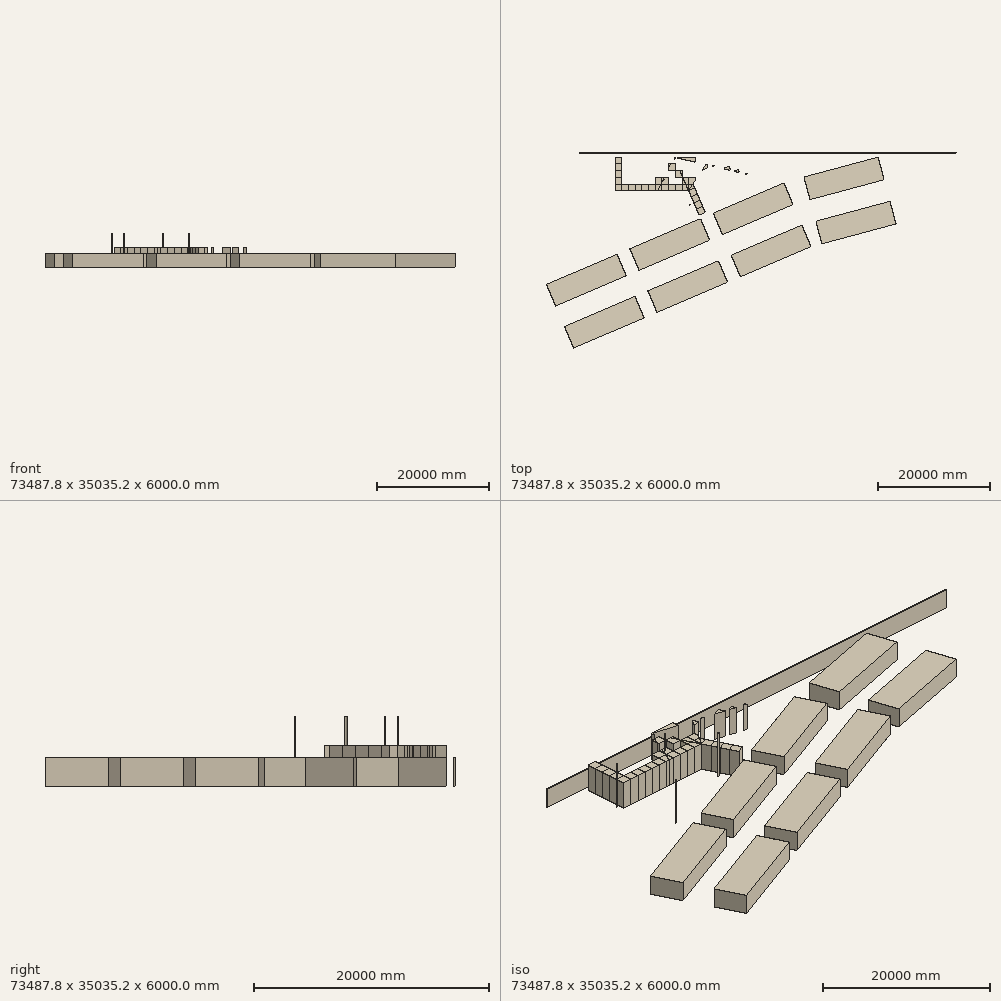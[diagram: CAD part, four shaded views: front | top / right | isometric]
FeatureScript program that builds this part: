
annotation { "Feature Type Name" : "Feature", "Feature Type Description" : "" }
export const myFeature = defineFeature(function(context is Context, id is Id, definition is map)
    precondition{}
    {
        {
            var Q0;
            Q0=qCreatedBy(makeId("Top.planeOp"),FACE);
            var sketch = newSketch(context, id + "F0", { "sketchPlane" : qUnion([Q0])});
            skLineSegment(sketch, "E0", {"start": v(21997.79, -272.27) * mm, "end": v(9345.13, -5680.4) * mm});
            skLineSegment(sketch, "E1", {"start": v(21997.79, -272.27) * mm, "end": v(20347.05, 3589.73) * mm});
            skLineSegment(sketch, "E2", {"start": v(20347.05, 3589.73) * mm, "end": v(7694.4, -1818.39) * mm});
            skLineSegment(sketch, "E3", {"start": v(7694.4, -1818.39) * mm, "end": v(9345.13, -5680.4) * mm});
            skLineSegment(sketch, "E4", {"start": v(7046.31, -6662.97) * mm, "end": v(5395.58, -2800.97) * mm});
            skLineSegment(sketch, "E5", {"start": v(5395.58, -2800.97) * mm, "end": v(-7257.08, -8209.09) * mm});
            skLineSegment(sketch, "E6", {"start": v(-7257.08, -8209.09) * mm, "end": v(-5606.35, -12071.09) * mm});
            skLineSegment(sketch, "E7", {"start": v(-7905.16, -13053.67) * mm, "end": v(-9555.9, -9191.67) * mm});
            skLineSegment(sketch, "E8", {"start": v(-9555.9, -9191.67) * mm, "end": v(-22208.56, -14599.78) * mm});
            skLineSegment(sketch, "E9", {"start": v(-22208.56, -14599.78) * mm, "end": v(-20557.82, -18461.79) * mm});
            skLineSegment(sketch, "E10.bottom", {"start": v(-9920.8, 8833.33) * mm, "end": v(51279.2, 8833.33) * mm});
            skLineSegment(sketch, "E10.top", {"start": v(-9920.8, 8233.33) * mm, "end": v(51279.2, 8233.33) * mm});
            skLineSegment(sketch, "E10.left", {"start": v(-9920.8, 8833.33) * mm, "end": v(-9920.8, 8233.33) * mm});
            skLineSegment(sketch, "E10.right", {"start": v(51279.2, 8833.33) * mm, "end": v(51279.2, 8233.33) * mm});
            skLineSegment(sketch, "E11", {"start": v(20347.05, 3589.73) * mm, "end": v(18362.24, 8233.33) * mm});
            skLineSegment(sketch, "E12", {"start": v(5395.58, -2800.97) * mm, "end": v(679.2, 8233.33) * mm});
            skLineSegment(sketch, "E13", {"start": v(-7257.08, -8209.09) * mm, "end": v(679.2, 8233.33) * mm});
            skLineSegment(sketch, "E14", {"start": v(679.2, 8233.33) * mm, "end": v(20347.05, 3589.73) * mm});
            skLineSegment(sketch, "E15", {"start": v(-9920.8, 8233.33) * mm, "end": v(13764.84, 8233.33) * mm});
            skLineSegment(sketch, "E16", {"start": v(13764.84, 8233.33) * mm, "end": v(16200.05, 2536) * mm});
            skLineSegment(sketch, "E17", {"start": v(5165.75, -2180.39) * mm, "end": v(3279.2, 2233.33) * mm});
            skLineSegment(sketch, "E18", {"start": v(3279.2, 2233.33) * mm, "end": v(-9920.8, 2233.33) * mm});
            skLineSegment(sketch, "E19", {"start": v(-9920.8, 2233.33) * mm, "end": v(-9920.8, 8233.33) * mm});
            skLineSegment(sketch, "E20", {"start": v(3279.2, 2233.33) * mm, "end": v(3279.2, 8233.33) * mm});
            skLineSegment(sketch, "E21", {"start": v(13764.84, 8233.33) * mm, "end": v(65121.17, 8233.33) * mm});
            skLineSegment(sketch, "E22", {"start": v(5165.75, -2180.39) * mm, "end": v(16200.05, 2536) * mm});
            skLineSegment(sketch, "E23.trimOffspring", {"start": v(-7905.16, -13053.67) * mm, "end": v(-20557.82, -18461.79) * mm});
            skLineSegment(sketch, "E24.trimOffspring", {"start": v(7046.31, -6662.97) * mm, "end": v(-5606.35, -12071.09) * mm});
            skLineSegment(sketch, "E25", {"start": v(-18985.7, -22139.89) * mm, "end": v(-17334.96, -26001.9) * mm});
            skLineSegment(sketch, "E26", {"start": v(-17334.96, -26001.9) * mm, "end": v(-4682.3, -20593.77) * mm});
            skLineSegment(sketch, "E27", {"start": v(-4682.3, -20593.77) * mm, "end": v(-6333.03, -16731.77) * mm});
            skLineSegment(sketch, "E28", {"start": v(-6333.03, -16731.77) * mm, "end": v(-18985.7, -22139.89) * mm});
            skLineSegment(sketch, "E29", {"start": v(-4034.22, -15749.19) * mm, "end": v(-2383.49, -19611.2) * mm});
            skLineSegment(sketch, "E30", {"start": v(-2383.49, -19611.2) * mm, "end": v(10269.17, -14203.08) * mm});
            skLineSegment(sketch, "E31", {"start": v(10269.17, -14203.08) * mm, "end": v(8618.44, -10341.07) * mm});
            skLineSegment(sketch, "E32", {"start": v(8618.44, -10341.07) * mm, "end": v(-4034.22, -15749.19) * mm});
            skLineSegment(sketch, "E33", {"start": v(10917.25, -9358.5) * mm, "end": v(12567.99, -13220.5) * mm});
            skLineSegment(sketch, "E34", {"start": v(12567.99, -13220.5) * mm, "end": v(25220.65, -7812.38) * mm});
            skLineSegment(sketch, "E35", {"start": v(25220.65, -7812.38) * mm, "end": v(23569.92, -3950.37) * mm});
            skLineSegment(sketch, "E36", {"start": v(23569.92, -3950.37) * mm, "end": v(10917.25, -9358.5) * mm});
            skLineSegment(sketch, "E37", {"start": v(26067.4, -3255.73) * mm, "end": v(27157.02, -7311.92) * mm});
            skLineSegment(sketch, "E38", {"start": v(27157.02, -7311.92) * mm, "end": v(40445.89, -3742.1) * mm});
            skLineSegment(sketch, "E39", {"start": v(40445.89, -3742.1) * mm, "end": v(39356.26, 314.1) * mm});
            skLineSegment(sketch, "E40", {"start": v(39356.26, 314.1) * mm, "end": v(26067.4, -3255.73) * mm});
            skLineSegment(sketch, "E41", {"start": v(14313.5, 6949.71) * mm, "end": v(3279.2, 2233.33) * mm});
            skLineSegment(sketch, "E42", {"start": v(5143.57, -2128.5) * mm, "end": v(5165.75, -2180.39) * mm});
            skLineSegment(sketch, "E43", {"start": v(51279.2, 8833.33) * mm, "end": v(35126.84, 8833.33) * mm});
            skPoint(sketch, "E44.start.orphan", {"position": v(39443, 8233.33) * mm});
            skLineSegment(sketch, "E45", {"start": v(23940.03, 4663.5) * mm, "end": v(25029.66, 607.32) * mm});
            skLineSegment(sketch, "E46", {"start": v(23940.03, 4663.5) * mm, "end": v(37228.9, 8233.33) * mm});
            skLineSegment(sketch, "E47", {"start": v(38318.53, 4177.14) * mm, "end": v(37228.9, 8233.33) * mm});
            skLineSegment(sketch, "E48", {"start": v(38318.53, 4177.14) * mm, "end": v(25029.66, 607.32) * mm});
            skPoint(sketch, "E49.end.orphan", {"position": v(31211.08, 8233.33) * mm});
            skCircle(sketch, "E50", {"center": v(-8104.42, -4710.23) * mm, "radius": 50.8 * mm});
            skCircle(sketch, "E51", {"center": v(-10266.87, 2993.64) * mm, "radius": 50.8 * mm});
            skCircle(sketch, "E52", {"center": v(-1108.7, 4123.22) * mm, "radius": 50.8 * mm});
            skCircle(sketch, "E53", {"center": v(535.54, -1097.3) * mm, "radius": 50.8 * mm});
            skCircle(sketch, "E54", {"center": v(3536.57, -320.23) * mm, "radius": 127 * mm});
            skLineSegment(sketch, "E55", {"start": v(-8720.8, 2233.33) * mm, "end": v(-8720.8, 8233.33) * mm});
            skLineSegment(sketch, "E56", {"start": v(-7520.8, 2233.33) * mm, "end": v(-7520.8, 8233.33) * mm});
            skLineSegment(sketch, "E57", {"start": v(-6320.8, 2233.33) * mm, "end": v(-6320.8, 8233.33) * mm});
            skLineSegment(sketch, "E58", {"start": v(-5120.8, 2233.33) * mm, "end": v(-5120.8, 8233.33) * mm});
            skLineSegment(sketch, "E59", {"start": v(-3920.8, 2233.33) * mm, "end": v(-3920.8, 8233.33) * mm});
            skLineSegment(sketch, "E60", {"start": v(-2720.8, 2233.33) * mm, "end": v(-2720.8, 8233.33) * mm});
            skLineSegment(sketch, "E61", {"start": v(-1520.8, 2233.33) * mm, "end": v(-1520.8, 8233.33) * mm});
            skLineSegment(sketch, "E62", {"start": v(-320.8, 2233.33) * mm, "end": v(-320.8, 8233.33) * mm});
            skLineSegment(sketch, "E63", {"start": v(879.2, 2233.33) * mm, "end": v(879.2, 8233.33) * mm});
            skLineSegment(sketch, "E64", {"start": v(2079.2, 2233.33) * mm, "end": v(2079.2, 8233.33) * mm});
            skLineSegment(sketch, "E65", {"start": v(-9920.8, 3433.33) * mm, "end": v(3279.2, 3433.33) * mm});
            skPoint(sketch, "E66.endSnap0", {"position": v(3279.2, 5233.33) * mm});
            skLineSegment(sketch, "E67", {"start": v(-9920.8, 8233.33) * mm, "end": v(-10520.8, 8233.33) * mm});
            skLineSegment(sketch, "E68", {"start": v(-10520.8, 8233.33) * mm, "end": v(-10520.8, 8833.33) * mm});
            skLineSegment(sketch, "E69", {"start": v(-10520.8, 8833.33) * mm, "end": v(-9920.8, 8833.33) * mm});
            skLineSegment(sketch, "E70", {"start": v(3279.2, 2233.33) * mm, "end": v(7239.73, 8233.33) * mm});
            skLineSegment(sketch, "E71", {"start": v(3279.2, 3433.33) * mm, "end": v(4071.3, 3433.33) * mm});
            skLineSegment(sketch, "E72", {"start": v(4071.3, 3433.33) * mm, "end": v(6269.18, -1708.75) * mm});
            skLineSegment(sketch, "E73.bottom", {"start": v(51279.2, 8833.33) * mm, "end": v(-16229.42, 8833.33) * mm});
            skLineSegment(sketch, "E73.top", {"start": v(51279.2, 9033.33) * mm, "end": v(-16229.42, 9033.33) * mm});
            skLineSegment(sketch, "E73.left", {"start": v(51279.2, 8833.33) * mm, "end": v(51279.2, 9033.33) * mm});
            skLineSegment(sketch, "E73.right", {"start": v(-16229.42, 8833.33) * mm, "end": v(-16229.42, 9033.33) * mm});
            skLineSegment(sketch, "E74.bottom", {"start": v(-16229.42, 9033.33) * mm, "end": v(-48265.6, 9033.33) * mm});
            skLineSegment(sketch, "E74.top", {"start": v(-16229.42, 8833.33) * mm, "end": v(-48265.6, 8833.33) * mm});
            skLineSegment(sketch, "E74.left", {"start": v(-16229.42, 9033.33) * mm, "end": v(-16229.42, 8833.33) * mm});
            skLineSegment(sketch, "E74.right", {"start": v(-48265.6, 9033.33) * mm, "end": v(-48265.6, 8833.33) * mm});
            skLineSegment(sketch, "E75", {"start": v(15728.41, 3639.42) * mm, "end": v(4664.16, -1089.76) * mm});
            skLineSegment(sketch, "E76", {"start": v(15256.77, 4742.85) * mm, "end": v(4222.47, 26.47) * mm});
            skLineSegment(sketch, "E77", {"start": v(14785.13, 5846.28) * mm, "end": v(3750.84, 1129.9) * mm});
            skLineSegment(sketch, "E78", {"start": v(13841.86, 8053.14) * mm, "end": v(4479.2, 4051.27) * mm});
            skLineSegment(sketch, "E79", {"start": v(-9920.8, 4633.33) * mm, "end": v(4479.2, 4633.33) * mm});
            skLineSegment(sketch, "E80", {"start": v(4479.2, 8233.33) * mm, "end": v(4479.2, 4051.27) * mm});
            skLineSegment(sketch, "E81", {"start": v(7372.61, -1237.11) * mm, "end": v(5014.42, 4280.04) * mm});
            skLineSegment(sketch, "E82", {"start": v(5679.2, 8233.33) * mm, "end": v(5679.2, 5869.2) * mm});
            skLineSegment(sketch, "E83", {"start": v(5679.2, 5869.2) * mm, "end": v(-9920.8, 5869.2) * mm});
            skLineSegment(sketch, "E84", {"start": v(-9920.8, 7069.2) * mm, "end": v(6471.3, 7069.2) * mm});
            skLineSegment(sketch, "E85", {"start": v(6471.3, 7069.2) * mm, "end": v(9612.46, -279.74) * mm});
            skLineSegment(sketch, "E86", {"start": v(5679.2, 5869.2) * mm, "end": v(11210.23, 8233.33) * mm});
            skLineSegment(sketch, "E87", {"start": v(7239.73, 8233.33) * mm, "end": v(10682.9, 177.8) * mm});
            skLineSegment(sketch, "E88", {"start": v(8544.75, 8233.33) * mm, "end": v(11786.33, 649.44) * mm});
            skLineSegment(sketch, "E89", {"start": v(9849.78, 8233.33) * mm, "end": v(12889.76, 1121.08) * mm});
            skLineSegment(sketch, "E90", {"start": v(11210.23, 8233.33) * mm, "end": v(14040.06, 1612.75) * mm});
            skLineSegment(sketch, "E91", {"start": v(12515.25, 8233.33) * mm, "end": v(15143.5, 2084.4) * mm});
            skLineSegment(sketch, "E92", {"start": v(8509.03, -751.37) * mm, "end": v(5679.2, 5869.2) * mm});
            skSolve(sketch);
        }
        {
            var Q0;
            Q0=makeQuery(id+"F0.imprint","IMPRINT",FACE,{"disambiguationData":[TD([[makeQuery(id+"F0.imprint","IMPRINT",EDGE,{"derivedFrom":sQuery(id+"F0.wireOp",EDGE,"E73.top")}),1.0]])]});
            extrude(context, id + "F1", {"entities" : qUnion([Q0]), "depth" : 2500 * mm, "offsetDistance" : 25 * mm});
        }
        {
            var Q0;
            Q0=makeQuery(id+"F0.imprint","IMPRINT",FACE,{"disambiguationData":[TD([[makeQuery(id+"F0.imprint","IMPRINT",EDGE,{"derivedFrom":sQuery(id+"F0.wireOp",EDGE,"E7")}),1.0]])]});
            var Q1;
            Q1=makeQuery(id+"F0.imprint","IMPRINT",FACE,{"disambiguationData":[TD([[makeQuery(id+"F0.imprint","IMPRINT",EDGE,{"derivedFrom":sQuery(id+"F0.wireOp",EDGE,"E4")}),1.0]])]});
            var Q2;
            Q2=makeQuery(id+"F0.imprint","IMPRINT",FACE,{"disambiguationData":[TD([[makeQuery(id+"F0.imprint","IMPRINT",EDGE,{"derivedFrom":sQuery(id+"F0.wireOp",EDGE,"E0")}),-1.0]])]});
            var Q3;
            Q3=makeQuery(id+"F0.imprint","IMPRINT",FACE,{"disambiguationData":[TD([[makeQuery(id+"F0.imprint","IMPRINT",EDGE,{"derivedFrom":sQuery(id+"F0.wireOp",EDGE,"E45")}),1.0]])]});
            var Q4;
            Q4=makeQuery(id+"F0.imprint","IMPRINT",FACE,{"disambiguationData":[TD([[makeQuery(id+"F0.imprint","IMPRINT",EDGE,{"derivedFrom":sQuery(id+"F0.wireOp",EDGE,"E37")}),1.0]])]});
            var Q5;
            Q5=makeQuery(id+"F0.imprint","IMPRINT",FACE,{"disambiguationData":[TD([[makeQuery(id+"F0.imprint","IMPRINT",EDGE,{"derivedFrom":sQuery(id+"F0.wireOp",EDGE,"E33")}),1.0]])]});
            var Q6;
            Q6=makeQuery(id+"F0.imprint","IMPRINT",FACE,{"disambiguationData":[TD([[makeQuery(id+"F0.imprint","IMPRINT",EDGE,{"derivedFrom":sQuery(id+"F0.wireOp",EDGE,"E29")}),1.0]])]});
            var Q7;
            Q7=makeQuery(id+"F0.imprint","IMPRINT",FACE,{"disambiguationData":[TD([[makeQuery(id+"F0.imprint","IMPRINT",EDGE,{"derivedFrom":sQuery(id+"F0.wireOp",EDGE,"E25")}),1.0]])]});
            extrude(context, id + "F2", {"entities" : qUnion([Q0, Q1, Q2, Q3, Q4, Q5, Q6, Q7]), "depth" : 2500 * mm, "offsetDistance" : 25 * mm});
        }
        {
            var Q0;
            {var subQ1=sQuery(id+"F0.wireOp",EDGE,"E15");var subQ3=sQuery(id+"F0.wireOp",EDGE,"E55");var subQ4=makeQuery(id+"F0.imprint","INTERSECT",VERTEX,{"derivedFrom":[subQ1,subQ3]});Q0=makeQuery(id+"F0.imprint","IMPRINT",FACE,{"disambiguationData":[TD([[makeQuery(id+"F0.imprint","IMPRINT",EDGE,{"disambiguationData":[TD([[subQ4,1.0]])],"derivedFrom":subQ3}),1.0]])]});}
            var Q1;
            {var subQ0=sQuery(id+"F0.wireOp",EDGE,"E55");var subQ1=sQuery(id+"F0.wireOp",EDGE,"E15");var subQ2=makeQuery(id+"F0.imprint","INTERSECT",VERTEX,{"derivedFrom":[subQ1,subQ0]});Q1=makeQuery(id+"F0.imprint","IMPRINT",FACE,{"disambiguationData":[TD([[makeQuery(id+"F0.imprint","IMPRINT",EDGE,{"disambiguationData":[TD([[subQ2,-1.0]])],"derivedFrom":subQ1}),-1.0]])]});}
            var Q2;
            {var subQ0=sQuery(id+"F0.wireOp",EDGE,"E56");var subQ1=sQuery(id+"F0.wireOp",EDGE,"E15");var subQ2=makeQuery(id+"F0.imprint","INTERSECT",VERTEX,{"derivedFrom":[subQ1,subQ0]});Q2=makeQuery(id+"F0.imprint","IMPRINT",FACE,{"disambiguationData":[TD([[makeQuery(id+"F0.imprint","IMPRINT",EDGE,{"disambiguationData":[TD([[subQ2,-1.0]])],"derivedFrom":subQ1}),-1.0]])]});}
            var Q3;
            {var subQ0=sQuery(id+"F0.wireOp",EDGE,"E57");var subQ1=sQuery(id+"F0.wireOp",EDGE,"E15");var subQ2=makeQuery(id+"F0.imprint","INTERSECT",VERTEX,{"derivedFrom":[subQ1,subQ0]});Q3=makeQuery(id+"F0.imprint","IMPRINT",FACE,{"disambiguationData":[TD([[makeQuery(id+"F0.imprint","IMPRINT",EDGE,{"disambiguationData":[TD([[subQ2,-1.0]])],"derivedFrom":subQ1}),-1.0]])]});}
            var Q4;
            {var subQ0=sQuery(id+"F0.wireOp",EDGE,"E58");var subQ1=sQuery(id+"F0.wireOp",EDGE,"E15");var subQ2=makeQuery(id+"F0.imprint","INTERSECT",VERTEX,{"derivedFrom":[subQ1,subQ0]});Q4=makeQuery(id+"F0.imprint","IMPRINT",FACE,{"disambiguationData":[TD([[makeQuery(id+"F0.imprint","IMPRINT",EDGE,{"disambiguationData":[TD([[subQ2,-1.0]])],"derivedFrom":subQ1}),-1.0]])]});}
            var Q5;
            {var subQ0=sQuery(id+"F0.wireOp",EDGE,"E59");var subQ1=sQuery(id+"F0.wireOp",EDGE,"E15");var subQ2=makeQuery(id+"F0.imprint","INTERSECT",VERTEX,{"derivedFrom":[subQ1,subQ0]});Q5=makeQuery(id+"F0.imprint","IMPRINT",FACE,{"disambiguationData":[TD([[makeQuery(id+"F0.imprint","IMPRINT",EDGE,{"disambiguationData":[TD([[subQ2,-1.0]])],"derivedFrom":subQ1}),-1.0]])]});}
            var Q6;
            {var subQ3=sQuery(id+"F0.wireOp",EDGE,"E13");var subQ7=sQuery(id+"F0.wireOp",EDGE,"E65");var subQ9=makeQuery(id+"F0.imprint","INTERSECT",VERTEX,{"derivedFrom":[subQ3,subQ7]});Q6=makeQuery(id+"F0.imprint","IMPRINT",FACE,{"disambiguationData":[TD([[makeQuery(id+"F0.imprint","IMPRINT",EDGE,{"disambiguationData":[TD([[subQ9,-1.0]])],"derivedFrom":subQ3}),1.0]])]});}
            var Q7;
            {var subQ0=sQuery(id+"F0.wireOp",EDGE,"E19");var subQ1=sQuery(id+"F0.wireOp",EDGE,"E18");var subQ2=makeQuery(id+"F0.imprint","INTERSECT",VERTEX,{"derivedFrom":[subQ1,subQ0]});Q7=makeQuery(id+"F0.imprint","IMPRINT",FACE,{"disambiguationData":[TD([[makeQuery(id+"F0.imprint","IMPRINT",EDGE,{"disambiguationData":[TD([[subQ2,1.0]])],"derivedFrom":subQ1}),-1.0]])]});}
            var Q8;
            {var subQ0=sQuery(id+"F0.wireOp",EDGE,"E55");var subQ1=sQuery(id+"F0.wireOp",EDGE,"E18");var subQ2=makeQuery(id+"F0.imprint","INTERSECT",VERTEX,{"derivedFrom":[subQ1,subQ0]});Q8=makeQuery(id+"F0.imprint","IMPRINT",FACE,{"disambiguationData":[TD([[makeQuery(id+"F0.imprint","IMPRINT",EDGE,{"disambiguationData":[TD([[subQ2,1.0]])],"derivedFrom":subQ1}),-1.0]])]});}
            var Q9;
            {var subQ0=sQuery(id+"F0.wireOp",EDGE,"E56");var subQ1=sQuery(id+"F0.wireOp",EDGE,"E18");var subQ2=makeQuery(id+"F0.imprint","INTERSECT",VERTEX,{"derivedFrom":[subQ1,subQ0]});Q9=makeQuery(id+"F0.imprint","IMPRINT",FACE,{"disambiguationData":[TD([[makeQuery(id+"F0.imprint","IMPRINT",EDGE,{"disambiguationData":[TD([[subQ2,1.0]])],"derivedFrom":subQ1}),-1.0]])]});}
            var Q10;
            {var subQ0=sQuery(id+"F0.wireOp",EDGE,"E57");var subQ1=sQuery(id+"F0.wireOp",EDGE,"E18");var subQ2=makeQuery(id+"F0.imprint","INTERSECT",VERTEX,{"derivedFrom":[subQ1,subQ0]});Q10=makeQuery(id+"F0.imprint","IMPRINT",FACE,{"disambiguationData":[TD([[makeQuery(id+"F0.imprint","IMPRINT",EDGE,{"disambiguationData":[TD([[subQ2,1.0]])],"derivedFrom":subQ1}),-1.0]])]});}
            var Q11;
            {var subQ0=sQuery(id+"F0.wireOp",EDGE,"E58");var subQ1=sQuery(id+"F0.wireOp",EDGE,"E18");var subQ2=makeQuery(id+"F0.imprint","INTERSECT",VERTEX,{"derivedFrom":[subQ1,subQ0]});Q11=makeQuery(id+"F0.imprint","IMPRINT",FACE,{"disambiguationData":[TD([[makeQuery(id+"F0.imprint","IMPRINT",EDGE,{"disambiguationData":[TD([[subQ2,1.0]])],"derivedFrom":subQ1}),-1.0]])]});}
            var Q12;
            {var subQ0=sQuery(id+"F0.wireOp",EDGE,"E59");var subQ1=sQuery(id+"F0.wireOp",EDGE,"E18");var subQ2=makeQuery(id+"F0.imprint","INTERSECT",VERTEX,{"derivedFrom":[subQ1,subQ0]});Q12=makeQuery(id+"F0.imprint","IMPRINT",FACE,{"disambiguationData":[TD([[makeQuery(id+"F0.imprint","IMPRINT",EDGE,{"disambiguationData":[TD([[subQ2,1.0]])],"derivedFrom":subQ1}),-1.0]])]});}
            var Q13;
            Q13=makeQuery(id+"F0.imprint","IMPRINT",FACE,{"disambiguationData":[TD([[makeQuery(id+"F0.imprint","IMPRINT",EDGE,{"derivedFrom":sQuery(id+"F0.wireOp",EDGE,"QqbQZRki-gGc1-FxrS-61yc-XFEHxBuBlKDp")}),1.0]])]});
            var Q14;
            {var subQ0=sQuery(id+"F0.wireOp",EDGE,"E70");var subQ1=sQuery(id+"F0.wireOp",EDGE,"E14");var subQ2=makeQuery(id+"F0.imprint","INTERSECT",VERTEX,{"derivedFrom":[subQ1,subQ0]});Q14=makeQuery(id+"F0.imprint","IMPRINT",FACE,{"disambiguationData":[TD([[makeQuery(id+"F0.imprint","IMPRINT",EDGE,{"disambiguationData":[TD([[subQ2,-1.0]])],"derivedFrom":subQ1}),-1.0]])]});}
            var Q15;
            {var subQ5=sQuery(id+"F0.wireOp",EDGE,"E71");Q15=makeQuery(id+"F0.imprint","IMPRINT",FACE,{"disambiguationData":[TD([[makeQuery(id+"F0.imprint","IMPRINT",EDGE,{"derivedFrom":subQ5}),1.0]])]});}
            var Q16;
            {var subQ1=sQuery(id+"F0.wireOp",EDGE,"E12");var subQ5=sQuery(id+"F0.wireOp",EDGE,"E65");var subQ9=makeQuery(id+"F0.imprint","INTERSECT",VERTEX,{"derivedFrom":[subQ1,subQ5]});Q16=makeQuery(id+"F0.imprint","IMPRINT",FACE,{"disambiguationData":[TD([[makeQuery(id+"F0.imprint","IMPRINT",EDGE,{"disambiguationData":[TD([[subQ9,-1.0]])],"derivedFrom":subQ1}),-1.0]])]});}
            var Q17;
            {var subQ0=sQuery(id+"F0.wireOp",EDGE,"E20");var subQ1=sQuery(id+"F0.wireOp",EDGE,"E14");var subQ2=makeQuery(id+"F0.imprint","INTERSECT",VERTEX,{"derivedFrom":[subQ1,subQ0]});Q17=makeQuery(id+"F0.imprint","IMPRINT",FACE,{"disambiguationData":[TD([[makeQuery(id+"F0.imprint","IMPRINT",EDGE,{"disambiguationData":[TD([[subQ2,-1.0]])],"derivedFrom":subQ1}),1.0]])]});}
            var Q18;
            {var subQ3=sQuery(id+"F0.wireOp",EDGE,"E14");var subQ5=sQuery(id+"F0.wireOp",EDGE,"E70");var subQ8=makeQuery(id+"F0.imprint","INTERSECT",VERTEX,{"derivedFrom":[subQ3,subQ5]});Q18=makeQuery(id+"F0.imprint","IMPRINT",FACE,{"disambiguationData":[TD([[makeQuery(id+"F0.imprint","IMPRINT",EDGE,{"disambiguationData":[TD([[subQ8,-1.0]])],"derivedFrom":subQ3}),1.0]])]});}
            var Q19;
            {var subQ0=sQuery(id+"F0.wireOp",EDGE,"E41");var subQ3=sQuery(id+"F0.wireOp",EDGE,"E14");var subQ4=makeQuery(id+"F0.imprint","INTERSECT",VERTEX,{"derivedFrom":[subQ3,subQ0]});Q19=makeQuery(id+"F0.imprint","IMPRINT",FACE,{"disambiguationData":[TD([[makeQuery(id+"F0.imprint","IMPRINT",EDGE,{"disambiguationData":[TD([[subQ4,-1.0]])],"derivedFrom":subQ3}),1.0]])]});}
            var Q20;
            {var subQ1=sQuery(id+"F0.wireOp",EDGE,"E17");Q20=makeQuery(id+"F0.imprint","IMPRINT",FACE,{"disambiguationData":[TD([[makeQuery(id+"F0.imprint","IMPRINT",EDGE,{"derivedFrom":subQ1}),-1.0]])]});}
            var Q21;
            {var subQ0=sQuery(id+"F0.wireOp",EDGE,"E61");var subQ1=sQuery(id+"F0.wireOp",EDGE,"E13");var subQ2=makeQuery(id+"F0.imprint","INTERSECT",VERTEX,{"derivedFrom":[subQ1,subQ0]});Q21=makeQuery(id+"F0.imprint","IMPRINT",FACE,{"disambiguationData":[TD([[makeQuery(id+"F0.imprint","IMPRINT",EDGE,{"disambiguationData":[TD([[subQ2,-1.0]])],"derivedFrom":subQ1}),1.0]])]});}
            var Q22;
            {var subQ0=sQuery(id+"F0.wireOp",EDGE,"E15");var subQ3=sQuery(id+"F0.wireOp",EDGE,"E62");var subQ5=makeQuery(id+"F0.imprint","INTERSECT",VERTEX,{"derivedFrom":[subQ0,subQ3]});Q22=makeQuery(id+"F0.imprint","IMPRINT",FACE,{"disambiguationData":[TD([[makeQuery(id+"F0.imprint","IMPRINT",EDGE,{"disambiguationData":[TD([[subQ5,1.0]])],"derivedFrom":subQ3}),-1.0]])]});}
            var Q23;
            {var subQ5=sQuery(id+"F0.wireOp",EDGE,"E62");var subQ6=sQuery(id+"F0.wireOp",EDGE,"E13");var subQ7=makeQuery(id+"F0.imprint","INTERSECT",VERTEX,{"derivedFrom":[subQ6,subQ5]});Q23=makeQuery(id+"F0.imprint","IMPRINT",FACE,{"disambiguationData":[TD([[makeQuery(id+"F0.imprint","IMPRINT",EDGE,{"disambiguationData":[TD([[subQ7,1.0]])],"derivedFrom":subQ5}),-1.0]])]});}
            var Q24;
            {var subQ0=sQuery(id+"F0.wireOp",EDGE,"E64");var subQ1=sQuery(id+"F0.wireOp",EDGE,"E12");var subQ2=makeQuery(id+"F0.imprint","INTERSECT",VERTEX,{"derivedFrom":[subQ1,subQ0]});Q24=makeQuery(id+"F0.imprint","IMPRINT",FACE,{"disambiguationData":[TD([[makeQuery(id+"F0.imprint","IMPRINT",EDGE,{"disambiguationData":[TD([[subQ2,-1.0]])],"derivedFrom":subQ1}),-1.0]])]});}
            var Q25;
            {var subQ0=sQuery(id+"F0.wireOp",EDGE,"E64");var subQ1=sQuery(id+"F0.wireOp",EDGE,"E14");var subQ2=makeQuery(id+"F0.imprint","INTERSECT",VERTEX,{"derivedFrom":[subQ1,subQ0]});Q25=makeQuery(id+"F0.imprint","IMPRINT",FACE,{"disambiguationData":[TD([[makeQuery(id+"F0.imprint","IMPRINT",EDGE,{"disambiguationData":[TD([[subQ2,-1.0]])],"derivedFrom":subQ1}),1.0]])]});}
            var Q26;
            {var subQ0=sQuery(id+"F0.wireOp",EDGE,"E18");var subQ1=sQuery(id+"F0.wireOp",EDGE,"E13");var subQ2=makeQuery(id+"F0.imprint","INTERSECT",VERTEX,{"derivedFrom":[subQ1,subQ0]});Q26=makeQuery(id+"F0.imprint","IMPRINT",FACE,{"disambiguationData":[TD([[makeQuery(id+"F0.imprint","IMPRINT",EDGE,{"disambiguationData":[TD([[subQ2,-1.0]])],"derivedFrom":subQ1}),1.0]])]});}
            var Q27;
            {var subQ0=sQuery(id+"F0.wireOp",EDGE,"E18");var subQ1=sQuery(id+"F0.wireOp",EDGE,"E13");var subQ2=makeQuery(id+"F0.imprint","INTERSECT",VERTEX,{"derivedFrom":[subQ1,subQ0]});Q27=makeQuery(id+"F0.imprint","IMPRINT",FACE,{"disambiguationData":[TD([[makeQuery(id+"F0.imprint","IMPRINT",EDGE,{"disambiguationData":[TD([[subQ2,-1.0]])],"derivedFrom":subQ1}),-1.0]])]});}
            var Q28;
            {var subQ0=sQuery(id+"F0.wireOp",EDGE,"E61");var subQ1=sQuery(id+"F0.wireOp",EDGE,"E18");var subQ2=makeQuery(id+"F0.imprint","INTERSECT",VERTEX,{"derivedFrom":[subQ1,subQ0]});Q28=makeQuery(id+"F0.imprint","IMPRINT",FACE,{"disambiguationData":[TD([[makeQuery(id+"F0.imprint","IMPRINT",EDGE,{"disambiguationData":[TD([[subQ2,1.0]])],"derivedFrom":subQ1}),-1.0]])]});}
            var Q29;
            {var subQ0=sQuery(id+"F0.wireOp",EDGE,"E62");var subQ1=sQuery(id+"F0.wireOp",EDGE,"E18");var subQ2=makeQuery(id+"F0.imprint","INTERSECT",VERTEX,{"derivedFrom":[subQ1,subQ0]});Q29=makeQuery(id+"F0.imprint","IMPRINT",FACE,{"disambiguationData":[TD([[makeQuery(id+"F0.imprint","IMPRINT",EDGE,{"disambiguationData":[TD([[subQ2,1.0]])],"derivedFrom":subQ1}),-1.0]])]});}
            var Q30;
            {var subQ0=sQuery(id+"F0.wireOp",EDGE,"E63");var subQ1=sQuery(id+"F0.wireOp",EDGE,"E18");var subQ2=makeQuery(id+"F0.imprint","INTERSECT",VERTEX,{"derivedFrom":[subQ1,subQ0]});Q30=makeQuery(id+"F0.imprint","IMPRINT",FACE,{"disambiguationData":[TD([[makeQuery(id+"F0.imprint","IMPRINT",EDGE,{"disambiguationData":[TD([[subQ2,1.0]])],"derivedFrom":subQ1}),-1.0]])]});}
            var Q31;
            {var subQ0=sQuery(id+"F0.wireOp",EDGE,"E18");var subQ1=sQuery(id+"F0.wireOp",EDGE,"E12");var subQ2=makeQuery(id+"F0.imprint","INTERSECT",VERTEX,{"derivedFrom":[subQ1,subQ0]});Q31=makeQuery(id+"F0.imprint","IMPRINT",FACE,{"disambiguationData":[TD([[makeQuery(id+"F0.imprint","IMPRINT",EDGE,{"disambiguationData":[TD([[subQ2,-1.0]])],"derivedFrom":subQ1}),1.0]])]});}
            var Q32;
            {var subQ0=sQuery(id+"F0.wireOp",EDGE,"E18");var subQ1=sQuery(id+"F0.wireOp",EDGE,"E12");var subQ2=makeQuery(id+"F0.imprint","INTERSECT",VERTEX,{"derivedFrom":[subQ1,subQ0]});Q32=makeQuery(id+"F0.imprint","IMPRINT",FACE,{"disambiguationData":[TD([[makeQuery(id+"F0.imprint","IMPRINT",EDGE,{"disambiguationData":[TD([[subQ2,-1.0]])],"derivedFrom":subQ1}),-1.0]])]});}
            var Q33;
            {var subQ3=sQuery(id+"F0.wireOp",EDGE,"E71");Q33=makeQuery(id+"F0.imprint","IMPRINT",FACE,{"disambiguationData":[TD([[makeQuery(id+"F0.imprint","IMPRINT",EDGE,{"derivedFrom":subQ3}),-1.0]])]});}
            var Q34;
            {var subQ1=sQuery(id+"F0.wireOp",EDGE,"E41");var subQ3=sQuery(id+"F0.wireOp",EDGE,"E72");var subQ4=makeQuery(id+"F0.imprint","INTERSECT",VERTEX,{"derivedFrom":[subQ1,subQ3]});Q34=makeQuery(id+"F0.imprint","IMPRINT",FACE,{"disambiguationData":[TD([[makeQuery(id+"F0.imprint","IMPRINT",EDGE,{"disambiguationData":[TD([[subQ4,1.0]])],"derivedFrom":subQ3}),-1.0]])]});}
            var Q35;
            {var subQ0=sQuery(id+"F0.wireOp",EDGE,"E65");var subQ1=sQuery(id+"F0.wireOp",EDGE,"E12");var subQ2=makeQuery(id+"F0.imprint","INTERSECT",VERTEX,{"derivedFrom":[subQ1,subQ0]});Q35=makeQuery(id+"F0.imprint","IMPRINT",FACE,{"disambiguationData":[TD([[makeQuery(id+"F0.imprint","IMPRINT",EDGE,{"disambiguationData":[TD([[subQ2,-1.0]])],"derivedFrom":subQ1}),1.0]])]});}
            var Q36;
            {var subQ0=sQuery(id+"F0.wireOp",EDGE,"E64");var subQ1=sQuery(id+"F0.wireOp",EDGE,"E12");var subQ2=makeQuery(id+"F0.imprint","INTERSECT",VERTEX,{"derivedFrom":[subQ1,subQ0]});Q36=makeQuery(id+"F0.imprint","IMPRINT",FACE,{"disambiguationData":[TD([[makeQuery(id+"F0.imprint","IMPRINT",EDGE,{"disambiguationData":[TD([[subQ2,-1.0]])],"derivedFrom":subQ1}),1.0]])]});}
            var Q37;
            Q37=makeQuery(id+"F0.imprint","IMPRINT",FACE,{"disambiguationData":[TD([[makeQuery(id+"F0.imprint","IMPRINT",EDGE,{"derivedFrom":sQuery(id+"F0.wireOp",EDGE,"E52")}),-1.0]])]});
            var Q38;
            {var subQ0=sQuery(id+"F0.wireOp",EDGE,"E65");var subQ1=sQuery(id+"F0.wireOp",EDGE,"E13");var subQ2=makeQuery(id+"F0.imprint","INTERSECT",VERTEX,{"derivedFrom":[subQ1,subQ0]});Q38=makeQuery(id+"F0.imprint","IMPRINT",FACE,{"disambiguationData":[TD([[makeQuery(id+"F0.imprint","IMPRINT",EDGE,{"disambiguationData":[TD([[subQ2,-1.0]])],"derivedFrom":subQ1}),-1.0]])]});}
            var Q39;
            {var subQ1=sQuery(id+"F0.wireOp",EDGE,"E12");var subQ3=sQuery(id+"F0.wireOp",EDGE,"E63");var subQ4=makeQuery(id+"F0.imprint","INTERSECT",VERTEX,{"derivedFrom":[subQ1,subQ3]});Q39=makeQuery(id+"F0.imprint","IMPRINT",FACE,{"disambiguationData":[TD([[makeQuery(id+"F0.imprint","IMPRINT",EDGE,{"disambiguationData":[TD([[subQ4,-1.0]])],"derivedFrom":subQ3}),1.0]])]});}
            var Q40;
            {var subQ0=sQuery(id+"F0.wireOp",EDGE,"E63");var subQ1=sQuery(id+"F0.wireOp",EDGE,"E14");var subQ2=makeQuery(id+"F0.imprint","INTERSECT",VERTEX,{"derivedFrom":[subQ1,subQ0]});Q40=makeQuery(id+"F0.imprint","IMPRINT",FACE,{"disambiguationData":[TD([[makeQuery(id+"F0.imprint","IMPRINT",EDGE,{"disambiguationData":[TD([[subQ2,-1.0]])],"derivedFrom":subQ1}),1.0]])]});}
            var Q41;
            {var subQ0=sQuery(id+"F0.wireOp",EDGE,"E15");var subQ3=sQuery(id+"F0.wireOp",EDGE,"E63");var subQ5=makeQuery(id+"F0.imprint","INTERSECT",VERTEX,{"derivedFrom":[subQ0,subQ3]});Q41=makeQuery(id+"F0.imprint","IMPRINT",FACE,{"disambiguationData":[TD([[makeQuery(id+"F0.imprint","IMPRINT",EDGE,{"disambiguationData":[TD([[subQ5,1.0]])],"derivedFrom":subQ3}),1.0]])]});}
            var Q42;
            {var subQ6=sQuery(id+"F0.wireOp",EDGE,"H4rWNhRk-xxGq-zGKP-ybOW-LqyXzqjWUUpq");Q42=makeQuery(id+"F0.imprint","IMPRINT",FACE,{"disambiguationData":[TD([[makeQuery(id+"F0.imprint","IMPRINT",EDGE,{"derivedFrom":subQ6}),1.0]])]});}
            var Q43;
            Q43=makeQuery(id+"F0.imprint","IMPRINT",FACE,{"disambiguationData":[TD([[makeQuery(id+"F0.imprint","IMPRINT",EDGE,{"derivedFrom":sQuery(id+"F0.wireOp",EDGE,"QqbQZRki-gGc1-FxrS-61yc-XFEHxBuBlKDp")}),-1.0]])]});
            var Q44;
            {var subQ0=sQuery(id+"F0.wireOp",EDGE,"KSq4bVeX-LUje-T9QJ-9OZV-ezZx69wXoiRM");var subQ1=sQuery(id+"F0.wireOp",EDGE,"E14");var subQ2=makeQuery(id+"F0.imprint","INTERSECT",VERTEX,{"derivedFrom":[subQ1,subQ0]});Q44=makeQuery(id+"F0.imprint","IMPRINT",FACE,{"disambiguationData":[TD([[makeQuery(id+"F0.imprint","IMPRINT",EDGE,{"disambiguationData":[TD([[subQ2,-1.0]])],"derivedFrom":subQ1}),1.0]])]});}
            extrude(context, id + "F3", {"entities" : qUnion([Q0, Q1, Q2, Q3, Q4, Q5, Q6, Q7, Q8, Q9, Q10, Q11, Q12, Q13, Q14, Q15, Q16, Q17, Q18, Q19, Q20, Q21, Q22, Q23, Q24, Q25, Q26, Q27, Q28, Q29, Q30, Q31, Q32, Q33, Q34, Q35, Q36, Q37, Q38, Q39, Q40, Q41, Q42, Q43, Q44]), "depth" : 3500 * mm, "offsetDistance" : 25 * mm});
        }
        {
            var Q0;
            Q0=makeQuery(id+"F0.imprint","IMPRINT",FACE,{"disambiguationData":[TD([[makeQuery(id+"F0.imprint","IMPRINT",EDGE,{"derivedFrom":sQuery(id+"F0.wireOp",EDGE,"E51")}),1.0]])]});
            var Q1;
            Q1=makeQuery(id+"F0.imprint","IMPRINT",FACE,{"disambiguationData":[TD([[makeQuery(id+"F0.imprint","IMPRINT",EDGE,{"derivedFrom":sQuery(id+"F0.wireOp",EDGE,"E52")}),1.0]])]});
            var Q2;
            Q2=makeQuery(id+"F0.imprint","IMPRINT",FACE,{"disambiguationData":[TD([[makeQuery(id+"F0.imprint","IMPRINT",EDGE,{"derivedFrom":sQuery(id+"F0.wireOp",EDGE,"E50")}),1.0]])]});
            extrude(context, id + "F4", {"entities" : qUnion([Q0, Q1, Q2]), "operationType" : NewBodyOperationType.ADD, "depth" : 6000 * mm, "offsetDistance" : 25 * mm});
        }
        {
            var Q0;
            Q0=makeQuery(id+"F0.imprint","IMPRINT",FACE,{"disambiguationData":[TD([[makeQuery(id+"F0.imprint","IMPRINT",EDGE,{"derivedFrom":sQuery(id+"F0.wireOp",EDGE,"E54")}),1.0]])]});
            extrude(context, id + "F5", {"entities" : qUnion([Q0]), "depth" : 6000 * mm, "offsetDistance" : 25 * mm});
        }
    });
